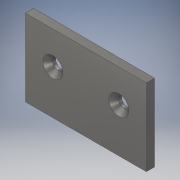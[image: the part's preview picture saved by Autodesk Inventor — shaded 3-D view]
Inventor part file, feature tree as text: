
AUTODESK INVENTOR PART (.ipt)
format: ipt  version: 2017 (Build 210142000, 142)  size: 106,496 bytes
history: native  units: in
note: dims shown in document units (in); Inventor stores cm internally (conversion verified against a paired STEP export)
features: hole x2, extrude x1, sketch x1
ambient origin geometry x8: Origin, YZ Plane, XZ Plane, XY Plane, X Axis, Y Axis, Z Axis, Center Point
bodies: Solid1 (feature_tree)
feature tree (4):
  extrude  "Extrusion1"  Depth=1.75in
  hole  "Hole1"  [1 undecoded]
  hole  "Hole2"  [1 undecoded]
  sketch  "Sketch1"  dims[d0=2.75in d1=1.75in d2=0.1875in d3=0.0in d4=1.0in d5=0.625in d6=0.25in d7=0.5in d8=0.452in d9=0.25in d10=0.5635in d11=0.75in d12=0.0in d13=1.0in d14=0.625in d15=0.25in d16=0.5in d17=0.452in d18=0.25in d19=0.5635in d20=0.75in d21=0.0in]
note: 2 required parameter values undecoded (feature->parameter linkage not recoverable at this tier; creation-order binding heuristic only, values carry confidence <= 0.55)
